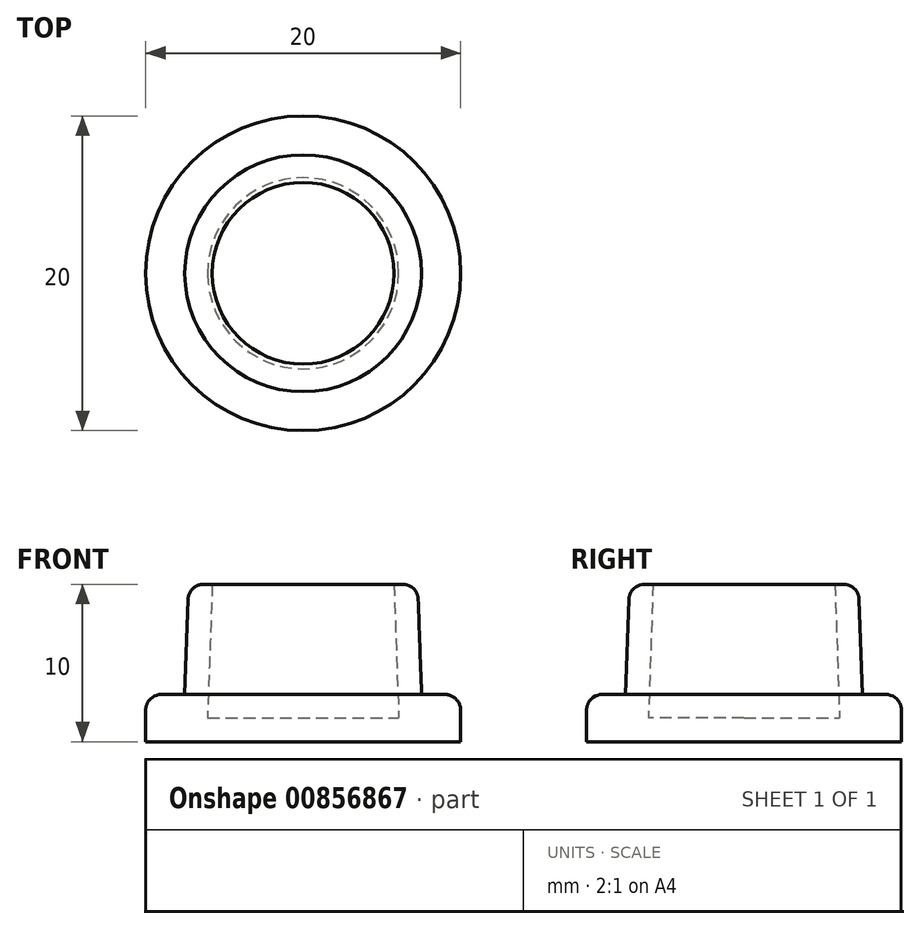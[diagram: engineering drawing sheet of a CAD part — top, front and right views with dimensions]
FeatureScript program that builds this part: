
annotation { "Feature Type Name" : "Feature", "Feature Type Description" : "" }
export const myFeature = defineFeature(function(context is Context, id is Id, definition is map)
    precondition{}
    {
        {
            var Q0;
            Q0=qCreatedBy(makeId("Right.planeOp"),FACE);
            var sketch = newSketch(context, id + "F0", { "sketchPlane" : qUnion([Q0])});
            skLineSegment(sketch, "E0", {"start": v(-7.52, 0) * mm, "end": v(-7.28, 7) * mm});
            skLineSegment(sketch, "E1", {"start": v(-7.28, 7) * mm, "end": v(0, 7) * mm});
            skLineSegment(sketch, "E2", {"start": v(0, 7) * mm, "end": v(0, 0) * mm});
            skLineSegment(sketch, "E3", {"start": v(0, 0) * mm, "end": v(-7.52, 0) * mm});
            skLineSegment(sketch, "E4.bottom", {"start": v(0, 0) * mm, "end": v(-10, 0) * mm});
            skLineSegment(sketch, "E4.top", {"start": v(0, -3) * mm, "end": v(-10, -3) * mm});
            skLineSegment(sketch, "E4.left", {"start": v(0, 0) * mm, "end": v(0, -3) * mm});
            skLineSegment(sketch, "E4.right", {"start": v(-10, 0) * mm, "end": v(-10, -3) * mm});
            skSolve(sketch);
        }
        {
            var Q0;
            Q0=makeQuery(id+"F0.imprint","IMPRINT",FACE,{"disambiguationData":[TD([[makeQuery(id+"F0.imprint","IMPRINT",EDGE,{"derivedFrom":sQuery(id+"F0.wireOp",EDGE,"E0")}),-1.0]])]});
            var Q1;
            Q1=makeQuery(id+"F0.imprint","IMPRINT",FACE,{"disambiguationData":[TD([[makeQuery(id+"F0.imprint","IMPRINT",EDGE,{"derivedFrom":sQuery(id+"F0.wireOp",EDGE,"E3")}),1.0]])]});
            var Q2;
            Q2=sQuery(id+"F0.wireOp",EDGE,"E2");
            revolve(context, id + "F1", {"surfaceOperationType" : NewSurfaceOperationType.NEW, "entities" : qUnion([Q0, Q1]), "axis" : qUnion([Q2]), "revolveType" : RevolveType.FULL});
        }
        {
            var Q0;
            Q0=makeQuery(id+"F1.opRevolve","SWEPT_EDGE",EDGE,{"disambiguationData":[OSD([sQuery(id+"F0.wireOp",EDGE,"E0"),sQuery(id+"F0.wireOp",EDGE,"E1")])]});
            var Q1;
            Q1=makeQuery(id+"F1.opRevolve","SWEPT_EDGE",EDGE,{"disambiguationData":[OSD([sQuery(id+"F0.wireOp",EDGE,"E4.bottom"),sQuery(id+"F0.wireOp",EDGE,"E4.right")])]});
            fillet(context, id + "F2", {"entities" : qUnion([Q0, Q1]), "radius" : 1 * mm, "tangentPropagation" : true, "allowEdgeOverflow" : false});
        }
        {
            var Q0;
            Q0=makeQuery(id+"F1.opRevolve","SWEPT_FACE",FACE,{"disambiguationData":[OSD([sQuery(id+"F0.wireOp",EDGE,"E1")])]});
            shell(context, id + "F3", {"entities" : qUnion([Q0]), "thickness" : 1.5 * mm});
        }
    });
